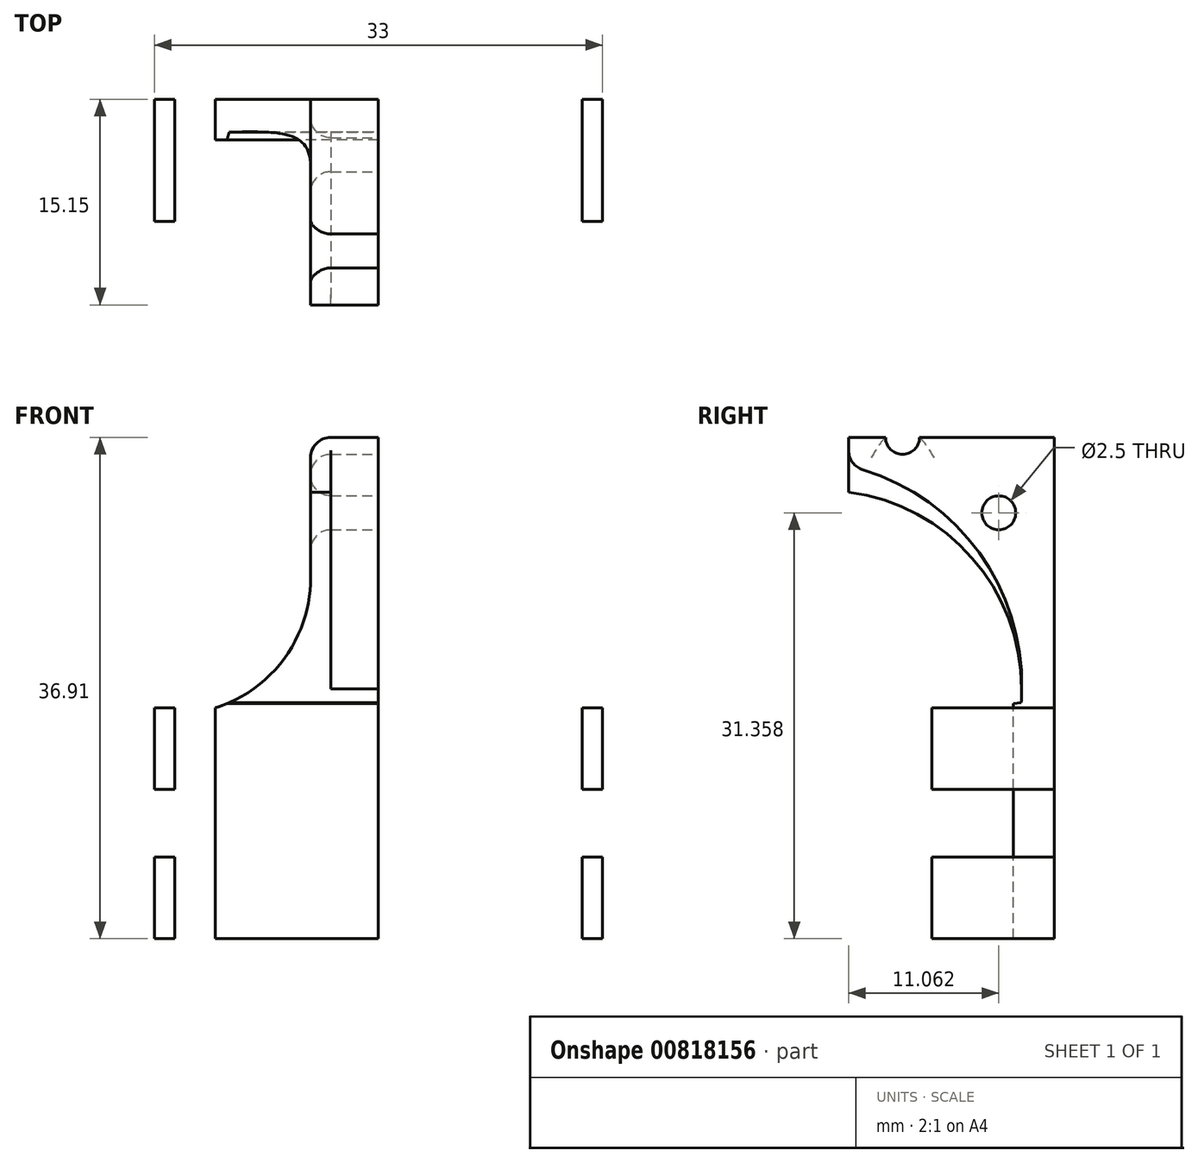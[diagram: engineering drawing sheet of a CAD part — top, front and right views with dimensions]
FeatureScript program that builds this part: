
annotation { "Feature Type Name" : "Feature", "Feature Type Description" : "" }
export const myFeature = defineFeature(function(context is Context, id is Id, definition is map)
    precondition{}
    {
        {
            var Q0;
            Q0=qCreatedBy(makeId("Front.planeOp"),FACE);
            var sketch = newSketch(context, id + "F0", { "sketchPlane" : qUnion([Q0])});
            skLineSegment(sketch, "E0.bottom", {"start": v(0, 0) * mm, "end": v(-15, 0) * mm});
            skLineSegment(sketch, "E0.top", {"start": v(0, 17) * mm, "end": v(-15, 17) * mm});
            skLineSegment(sketch, "E0.left", {"start": v(0, 0) * mm, "end": v(0, 17) * mm});
            skLineSegment(sketch, "E0.right", {"start": v(-15, 0) * mm, "end": v(-15, 17) * mm});
            skLineSegment(sketch, "E1.bottom", {"start": v(0, 17) * mm, "end": v(-7.5, 17) * mm});
            skLineSegment(sketch, "E2.bottom", {"start": v(-15, 0) * mm, "end": v(-12, 0) * mm});
            skLineSegment(sketch, "E2.top", {"start": v(-15, 17) * mm, "end": v(-12, 17) * mm});
            skLineSegment(sketch, "E2.right", {"start": v(-12, 0) * mm, "end": v(-12, 17) * mm});
            skLineSegment(sketch, "E3.bottom", {"start": v(-15, 0) * mm, "end": v(-16.5, 0) * mm});
            skLineSegment(sketch, "E3.top", {"start": v(-15, 6) * mm, "end": v(-16.5, 6) * mm});
            skLineSegment(sketch, "E3.left", {"start": v(-15, 0) * mm, "end": v(-15, 6) * mm});
            skLineSegment(sketch, "E3.right", {"start": v(-16.5, 0) * mm, "end": v(-16.5, 6) * mm});
            skLineSegment(sketch, "E4.bottom", {"start": v(-15, 17) * mm, "end": v(-16.5, 17) * mm});
            skLineSegment(sketch, "E4.top", {"start": v(-15, 11) * mm, "end": v(-16.5, 11) * mm});
            skLineSegment(sketch, "E4.left", {"start": v(-15, 17) * mm, "end": v(-15, 11) * mm});
            skLineSegment(sketch, "E4.right", {"start": v(-16.5, 17) * mm, "end": v(-16.5, 11) * mm});
            skSolve(sketch);
        }
        {
            var Q0;
            Q0=makeQuery(id+"F0.imprint","IMPRINT",FACE,{"disambiguationData":[TD([[makeQuery(id+"F0.imprint","IMPRINT",EDGE,{"derivedFrom":sQuery(id+"F0.wireOp",EDGE,"E2.bottom")}),1.0]])]});
            var Q1;
            Q1=makeQuery(id+"F0.imprint","IMPRINT",FACE,{"disambiguationData":[TD([[makeQuery(id+"F0.imprint","IMPRINT",EDGE,{"derivedFrom":sQuery(id+"F0.wireOp",EDGE,"E4.bottom")}),1.0]])]});
            var Q2;
            Q2=makeQuery(id+"F0.imprint","IMPRINT",FACE,{"disambiguationData":[TD([[makeQuery(id+"F0.imprint","IMPRINT",EDGE,{"derivedFrom":sQuery(id+"F0.wireOp",EDGE,"E3.bottom")}),-1.0]])]});
            extrude(context, id + "F1", {"entities" : qUnion([Q0, Q1, Q2]), "depth" : 9 * mm, "offsetDistance" : 25 * mm});
        }
        {
            var Q0;
            Q0=makeQuery(id+"F0.imprint","IMPRINT",FACE,{"disambiguationData":[TD([[makeQuery(id+"F0.imprint","IMPRINT",EDGE,{"derivedFrom":sQuery(id+"F0.wireOp",EDGE,"E0.bottom")}),-1.0]])]});
            extrude(context, id + "F2", {"entities" : qUnion([Q0]), "operationType" : NewBodyOperationType.ADD, "depth" : 3 * mm, "offsetDistance" : 25 * mm});
        }
        {
            var Q0;
            Q0=qCreatedBy(makeId("Right.planeOp"),FACE);
            var sketch = newSketch(context, id + "F3", { "sketchPlane" : qUnion([Q0])});
            skLineSegment(sketch, "E5", {"start": v(0, 16.91) * mm, "end": v(0, 36.91) * mm});
            skLineSegment(sketch, "E6", {"start": v(0, 36.91) * mm, "end": v(-18.25, 36.91) * mm});
            skLineSegment(sketch, "E7", {"start": v(0, 16.91) * mm, "end": v(-2.5, 16.91) * mm});
            skArc(sketch, "E8", {"start": v(-2.5, 16.91) * mm, "mid": v(-6.9, 30.08) * mm, "end": v(-19.81, 35.2) * mm});
            skLineSegment(sketch, "E9", {"start": v(-15.15, 36.91) * mm, "end": v(-15.15, 34.8) * mm});
            skCircle(sketch, "E10", {"center": v(-4.09, 31.36) * mm, "radius": 1.25 * mm});
            skCircle(sketch, "E11", {"center": v(-11.17, 36.91) * mm, "radius": 1.25 * mm});
            skArc(sketch, "E12", {"start": v(-2.47, 16.91) * mm, "mid": v(-5.58, 27.47) * mm, "end": v(-15.15, 32.88) * mm});
            skLineSegment(sketch, "E13", {"start": v(-15.15, 34.8) * mm, "end": v(-15.15, 32.88) * mm});
            skSolve(sketch);
        }
        {
            var Q0;
            {var subQ5=sQuery(id+"F3.wireOp",EDGE,"E5");Q0=makeQuery(id+"F3.imprint","IMPRINT",FACE,{"disambiguationData":[TD([[makeQuery(id+"F3.imprint","IMPRINT",EDGE,{"derivedFrom":subQ5}),1.0]])]});}
            extrude(context, id + "F4", {"entities" : qUnion([Q0]), "operationType" : NewBodyOperationType.ADD, "depth" : -3.5 * mm, "offsetDistance" : 25 * mm});
        }
        {
            var Q0;
            {var subQ1=sQuery(id+"F3.wireOp",EDGE,"E5");Q0=makeQuery(id+"F3.imprint","IMPRINT",FACE,{"disambiguationData":[TD([[makeQuery(id+"F3.imprint","IMPRINT",EDGE,{"derivedFrom":subQ1}),1.0]])]});}
            var Q1;
            {var subQ0=sQuery(id+"F3.wireOp",EDGE,"E13");Q1=makeQuery(id+"F3.imprint","IMPRINT",FACE,{"disambiguationData":[TD([[makeQuery(id+"F3.imprint","IMPRINT",EDGE,{"derivedFrom":subQ0}),1.0]])]});}
            extrude(context, id + "F5", {"entities" : qUnion([Q0, Q1]), "operationType" : NewBodyOperationType.ADD, "depth" : -5 * mm, "offsetDistance" : 25 * mm, "hasSecondDirection" : true, "secondDirectionOppositeDirection" : true, "secondDirectionDepth" : 3.5 * mm});
        }
        {
            var Q0;
            Q0=makeQuery(id+"F1.opExtrude","SWEPT_BODY",BODY,{"disambiguationData":[OSD([sQuery(id+"F0.wireOp",EDGE,"E2.bottom"),sQuery(id+"F0.wireOp",EDGE,"E2.top"),sQuery(id+"F0.wireOp",EDGE,"E0.right"),sQuery(id+"F0.wireOp",EDGE,"E2.right"),sQuery(id+"F0.wireOp",EDGE,"E3.bottom"),sQuery(id+"F0.wireOp",EDGE,"E3.top"),sQuery(id+"F0.wireOp",EDGE,"E3.right"),sQuery(id+"F0.wireOp",EDGE,"E4.bottom"),sQuery(id+"F0.wireOp",EDGE,"E4.top"),sQuery(id+"F0.wireOp",EDGE,"E4.right")])]});
            var Q1;
            Q1=qCreatedBy(makeId("Right.planeOp"),FACE);
            mirror(context, id + "F6", {"operationType" : NewBodyOperationType.ADD, "entities" : qUnion([Q0]), "mirrorPlane" : qUnion([Q1])});
        }
        {
            var Q0;
            Q0=makeQuery(id+"F5.boolean.opBoolean","INTERSECT",EDGE,{"derivedFrom":[makeQuery(id+"F2.boolean.opBoolean","MERGE",FACE,{"derivedFrom":[makeQuery(id+"F1.opExtrude","SWEPT_FACE",FACE,{"disambiguationData":[OSD([sQuery(id+"F0.wireOp",EDGE,"E2.top"),sQuery(id+"F0.wireOp",EDGE,"E4.bottom")])]}),makeQuery(id+"F2.opExtrude","SWEPT_FACE",FACE,{"disambiguationData":[OSD([sQuery(id+"F0.wireOp",EDGE,"E0.top"),sQuery(id+"F0.wireOp",EDGE,"E1.bottom")])]})]}),makeQuery(id+"F5.opExtrude","CAP_FACE",FACE,{"disambiguationData":[OSD([sQuery(id+"F3.wireOp",EDGE,"E5"),sQuery(id+"F3.wireOp",EDGE,"E6"),sQuery(id+"F3.wireOp",EDGE,"E7"),sQuery(id+"F3.wireOp",EDGE,"E9"),sQuery(id+"F3.wireOp",EDGE,"E10"),sQuery(id+"F3.wireOp",EDGE,"E11"),sQuery(id+"F3.wireOp",EDGE,"E12"),sQuery(id+"F3.wireOp",EDGE,"E13")])],"isStart":false})]});
            var Q1;
            Q1=makeQuery(id+"F6.opPattern","COPY",EDGE,{"derivedFrom":makeQuery(id+"F5.boolean.opBoolean","INTERSECT",EDGE,{"derivedFrom":[makeQuery(id+"F2.boolean.opBoolean","MERGE",FACE,{"derivedFrom":[makeQuery(id+"F1.opExtrude","SWEPT_FACE",FACE,{"disambiguationData":[OSD([sQuery(id+"F0.wireOp",EDGE,"E2.top"),sQuery(id+"F0.wireOp",EDGE,"E4.bottom")])]}),makeQuery(id+"F2.opExtrude","SWEPT_FACE",FACE,{"disambiguationData":[OSD([sQuery(id+"F0.wireOp",EDGE,"E0.top"),sQuery(id+"F0.wireOp",EDGE,"E1.bottom")])]})]}),makeQuery(id+"F5.opExtrude","CAP_FACE",FACE,{"disambiguationData":[OSD([sQuery(id+"F3.wireOp",EDGE,"E5"),sQuery(id+"F3.wireOp",EDGE,"E6"),sQuery(id+"F3.wireOp",EDGE,"E7"),sQuery(id+"F3.wireOp",EDGE,"E9"),sQuery(id+"F3.wireOp",EDGE,"E10"),sQuery(id+"F3.wireOp",EDGE,"E11"),sQuery(id+"F3.wireOp",EDGE,"E12"),sQuery(id+"F3.wireOp",EDGE,"E13")])],"isStart":false})]}),"instanceName":"1"});
            fillet(context, id + "F7", {"entities" : qUnion([Q0, Q1]), "radius" : 10 * mm, "tangentPropagation" : true, "allowEdgeOverflow" : false});
        }
        {
            var Q0;
            Q0=makeQuery(id+"F5.opExtrude","CAP_EDGE",EDGE,{"disambiguationData":[OSD([sQuery(id+"F3.wireOp",EDGE,"E10")])],"isStart":false});
            var Q1;
            Q1=makeQuery(id+"F5.opExtrude","CAP_EDGE",EDGE,{"disambiguationData":[OSD([sQuery(id+"F3.wireOp",EDGE,"E11")])],"isStart":false});
            var Q2;
            Q2=makeQuery(id+"F6.opPattern","COPY",EDGE,{"derivedFrom":makeQuery(id+"F5.opExtrude","CAP_EDGE",EDGE,{"disambiguationData":[OSD([sQuery(id+"F3.wireOp",EDGE,"E10")])],"isStart":false}),"instanceName":"1"});
            var Q3;
            Q3=makeQuery(id+"F6.opPattern","COPY",EDGE,{"derivedFrom":makeQuery(id+"F5.opExtrude","CAP_EDGE",EDGE,{"disambiguationData":[OSD([sQuery(id+"F3.wireOp",EDGE,"E11")])],"isStart":false}),"instanceName":"1"});
            var Q4;
            Q4=makeQuery(id+"F1.opExtrude","CAP_EDGE",EDGE,{"disambiguationData":[OSD([sQuery(id+"F0.wireOp",EDGE,"E0.right")])],"isStart":false});
            var Q5;
            Q5=makeQuery(id+"F6.opPattern","COPY",EDGE,{"derivedFrom":makeQuery(id+"F1.opExtrude","CAP_EDGE",EDGE,{"disambiguationData":[OSD([sQuery(id+"F0.wireOp",EDGE,"E0.right")])],"isStart":false}),"instanceName":"1"});
            var Q6;
            Q6=makeQuery(id+"F1.opExtrude","SWEPT_EDGE",EDGE,{"disambiguationData":[OSD([sQuery(id+"F0.wireOp",EDGE,"E4.bottom"),sQuery(id+"F0.wireOp",EDGE,"E4.right")])]});
            var Q7;
            Q7=makeQuery(id+"F1.opExtrude","SWEPT_EDGE",EDGE,{"disambiguationData":[OSD([sQuery(id+"F0.wireOp",EDGE,"E3.bottom"),sQuery(id+"F0.wireOp",EDGE,"E3.right")])]});
            var Q8;
            Q8=makeQuery(id+"F6.opPattern","COPY",EDGE,{"derivedFrom":makeQuery(id+"F1.opExtrude","SWEPT_EDGE",EDGE,{"disambiguationData":[OSD([sQuery(id+"F0.wireOp",EDGE,"E3.bottom"),sQuery(id+"F0.wireOp",EDGE,"E3.right")])]}),"instanceName":"1"});
            var Q9;
            Q9=makeQuery(id+"F6.opPattern","COPY",EDGE,{"derivedFrom":makeQuery(id+"F1.opExtrude","SWEPT_EDGE",EDGE,{"disambiguationData":[OSD([sQuery(id+"F0.wireOp",EDGE,"E4.bottom"),sQuery(id+"F0.wireOp",EDGE,"E4.right")])]}),"instanceName":"1"});
            var Q10;
            {var subQ0=sQuery(id+"F3.wireOp",EDGE,"E6");Q10=makeQuery(id+"F6.opPattern","COPY",EDGE,{"derivedFrom":makeQuery(id+"F5.opExtrude","CAP_EDGE",EDGE,{"disambiguationData":[OSD([subQ0]),TDD([makeQuery(id+"F3.imprint","IMPRINT",EDGE,{"disambiguationData":[TD([[makeQuery(id+"F3.imprint","INTERSECT",VERTEX,{"derivedFrom":[sQuery(id+"F3.wireOp",EDGE,"E5"),subQ0]}),-1.0]])],"derivedFrom":subQ0})])],"isStart":false}),"instanceName":"1"});}
            var Q11;
            {var subQ0=sQuery(id+"F3.wireOp",EDGE,"E6");Q11=makeQuery(id+"F5.opExtrude","CAP_EDGE",EDGE,{"disambiguationData":[OSD([subQ0]),TDD([makeQuery(id+"F3.imprint","IMPRINT",EDGE,{"disambiguationData":[TD([[makeQuery(id+"F3.imprint","INTERSECT",VERTEX,{"derivedFrom":[sQuery(id+"F3.wireOp",EDGE,"E5"),subQ0]}),-1.0]])],"derivedFrom":subQ0})])],"isStart":false});}
            var Q12;
            {var subQ0=sQuery(id+"F3.wireOp",EDGE,"E6");Q12=makeQuery(id+"F5.opExtrude","CAP_EDGE",EDGE,{"disambiguationData":[OSD([subQ0]),TDD([makeQuery(id+"F3.imprint","IMPRINT",EDGE,{"disambiguationData":[TD([[makeQuery(id+"F3.imprint","INTERSECT",VERTEX,{"derivedFrom":[subQ0,sQuery(id+"F3.wireOp",EDGE,"E9")]}),1.0]])],"derivedFrom":subQ0})])],"isStart":false});}
            var Q13;
            {var subQ0=sQuery(id+"F3.wireOp",EDGE,"E6");Q13=makeQuery(id+"F6.opPattern","COPY",EDGE,{"derivedFrom":makeQuery(id+"F5.opExtrude","CAP_EDGE",EDGE,{"disambiguationData":[OSD([subQ0]),TDD([makeQuery(id+"F3.imprint","IMPRINT",EDGE,{"disambiguationData":[TD([[makeQuery(id+"F3.imprint","INTERSECT",VERTEX,{"derivedFrom":[subQ0,sQuery(id+"F3.wireOp",EDGE,"E9")]}),1.0]])],"derivedFrom":subQ0})])],"isStart":false}),"instanceName":"1"});}
            var Q14;
            {var subQ0=makeQuery(id+"F4.opExtrude","SWEPT_EDGE",EDGE,{"disambiguationData":[OSD([sQuery(id+"F3.wireOp",EDGE,"E8"),sQuery(id+"F3.wireOp",EDGE,"E9"),sQuery(id+"F3.wireOp",EDGE,"E13")])]});Q14=makeQuery(id+"F6.boolean.opBoolean","MERGE",EDGE,{"derivedFrom":[subQ0,makeQuery(id+"F6.opPattern","COPY",EDGE,{"derivedFrom":subQ0,"instanceName":"1"})]});}
            fillet(context, id + "F8", {"entities" : qUnion([Q0, Q1, Q2, Q3, Q4, Q5, Q6, Q7, Q8, Q9, Q10, Q11, Q12, Q13, Q14]), "radius" : 1.5 * mm, "tangentPropagation" : true, "allowEdgeOverflow" : false});
        }
        {
            var Q0;
            {var subQ0=makeQuery(id+"F5.boolean.opBoolean","INTERSECT",EDGE,{"derivedFrom":[makeQuery(id+"F2.boolean.opBoolean","MERGE",FACE,{"derivedFrom":[makeQuery(id+"F1.opExtrude","SWEPT_FACE",FACE,{"disambiguationData":[OSD([sQuery(id+"F0.wireOp",EDGE,"E2.top"),sQuery(id+"F0.wireOp",EDGE,"E4.bottom")])]}),makeQuery(id+"F2.opExtrude","SWEPT_FACE",FACE,{"disambiguationData":[OSD([sQuery(id+"F0.wireOp",EDGE,"E0.top"),sQuery(id+"F0.wireOp",EDGE,"E1.bottom")])]})]}),makeQuery(id+"F5.opExtrude","SWEPT_FACE",FACE,{"disambiguationData":[OSD([sQuery(id+"F3.wireOp",EDGE,"E12")])]})]});Q0=makeQuery(id+"F6.boolean.opBoolean","MERGE",EDGE,{"derivedFrom":[subQ0,makeQuery(id+"F6.opPattern","COPY",EDGE,{"derivedFrom":subQ0,"instanceName":"1"})]});}
            chamfer(context, id + "F9", {"entities" : qUnion([Q0]), "chamferType" : ChamferType.TWO_OFFSETS, "width1" : 0.3 * mm, "oppositeDirection" : false, "width2" : 3 * mm, "tangentPropagation" : true});
        }
    });
